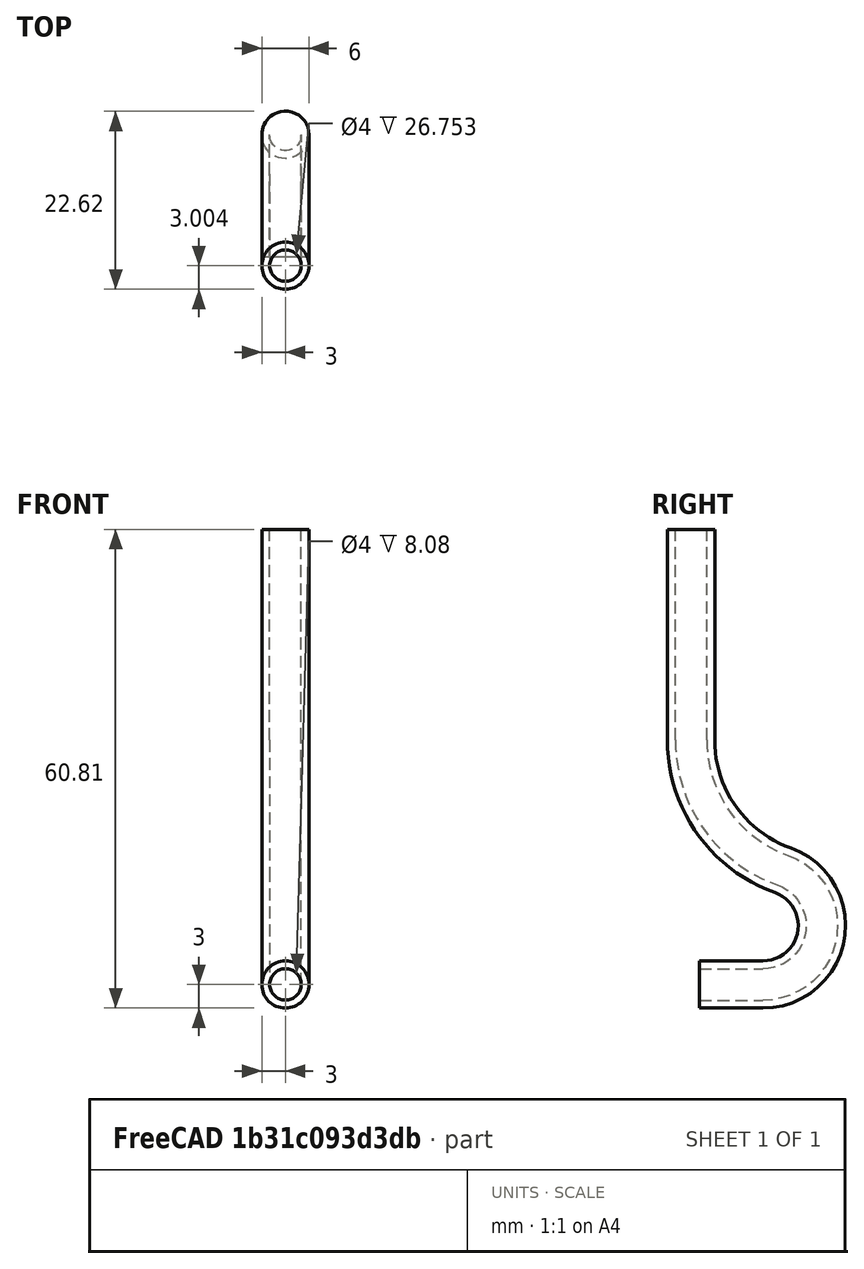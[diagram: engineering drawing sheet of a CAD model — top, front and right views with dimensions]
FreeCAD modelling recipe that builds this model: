
FCSTD DOCUMENT  (FreeCAD 0.19R24267 (Git))
Label: silicone_tube
License: All rights reserved
LicenseURL: http://en.wikipedia.org/wiki/All_rights_reserved
objects: Sketcher::SketchObject×2, PartDesign::AdditivePipe×1, PartDesign::Body×1, PartDesign::CoordinateSystem×1, App::Part×1
note: 6 computed .brp shape members not serialized (recipe doc carries the construction recipe); baked Part::Feature solids carry a one-line shape summary decoded from their .brp

FEATURE [Sketcher::SketchObject] Sketch085
  FullyConstrained = false
  MapMode = 5
  Placement = pos=(0,0,0) rot=(0.57735,0.57735,0.57735;2.0944rad)
  Support = -> [YZ_Plane099]
  sketch-geometry (4):
    g0: LineSegment StartX=0 StartY=0 StartZ=0 EndX=8.08004 EndY=0 EndZ=0
    g1: ArcOfCircle CenterX=8.08004 CenterY=7.47139 CenterZ=0 NormalX=0 NormalY=0 NormalZ=1 AngleXU=0 Radius=7.47139 StartAngle=4.71239 EndAngle=7.5108
    g2: ArcOfCircle CenterX=16.5072 CenterY=31.0557 CenterZ=0 NormalX=0 NormalY=0 NormalZ=1 AngleXU=0 Radius=17.5733 StartAngle=3.14159 EndAngle=4.36921
    g3: LineSegment StartX=-1.06608 StartY=31.0557 StartZ=0 EndX=-1.06608 EndY=57.8085 EndZ=0
  constraints (6):
    c: Coincident(g0,g-1)
    c: Horizontal(g0)
    c: Tangent(g3,g2) = 1.5708
    c: Tangent(g2,g1) = 1.5708
    c: Tangent(g1,g0) = -1.5708
    c: Vertical(g3)
FEATURE [Sketcher::SketchObject] Sketch086
  FullyConstrained = false
  MapMode = 5
  Placement = pos=(0,0,0) rot=(1,0,0;1.5708rad)
  Support = -> [XZ_Plane099]
  sketch-geometry (2):
    g0: Circle CenterX=0 CenterY=0 CenterZ=0 NormalX=0 NormalY=0 NormalZ=1 AngleXU=0 Radius=2
    g1: Circle CenterX=0 CenterY=0 CenterZ=0 NormalX=0 NormalY=0 NormalZ=1 AngleXU=0 Radius=3
  constraints (4):
    c: Coincident(g0,g-1)
    c: Coincident(g1,g0)
    c: Diameter(g1) = 6
    c: Diameter(g0) = 4
FEATURE [PartDesign::AdditivePipe] AdditivePipe002
  AuxilleryCurvelinear = true
  AuxillerySpineTangent = false
  Binormal = (0,0,0)
  Mode = 2
  Placement = pos=(0,0,0) rot=(1,0,0;1.5708rad)
  Profile = -> Sketch086
  Spine = -> Sketch085
  SpineTangent = false
  Transformation = 0
  Transition = 0
FEATURE [PartDesign::Body] Body032  label="Body"
  Group = -> [Sketch085,Sketch086,AdditivePipe002]
  Origin = -> Origin099
  Tip = -> AdditivePipe002
FEATURE [PartDesign::CoordinateSystem] LCS_1
  AttacherType = Attacher::AttachEngine3D
  MapMode = 11
  Placement = pos=(0,0,0) rot=(0.57735,-0.57735,0.57735;2.0944rad)
  Support = -> [AdditivePipe002]
FEATURE [App::Part] Part  label="silicone_tube"
  Group = -> [Body032,LCS_1]
  Origin = -> Origin
